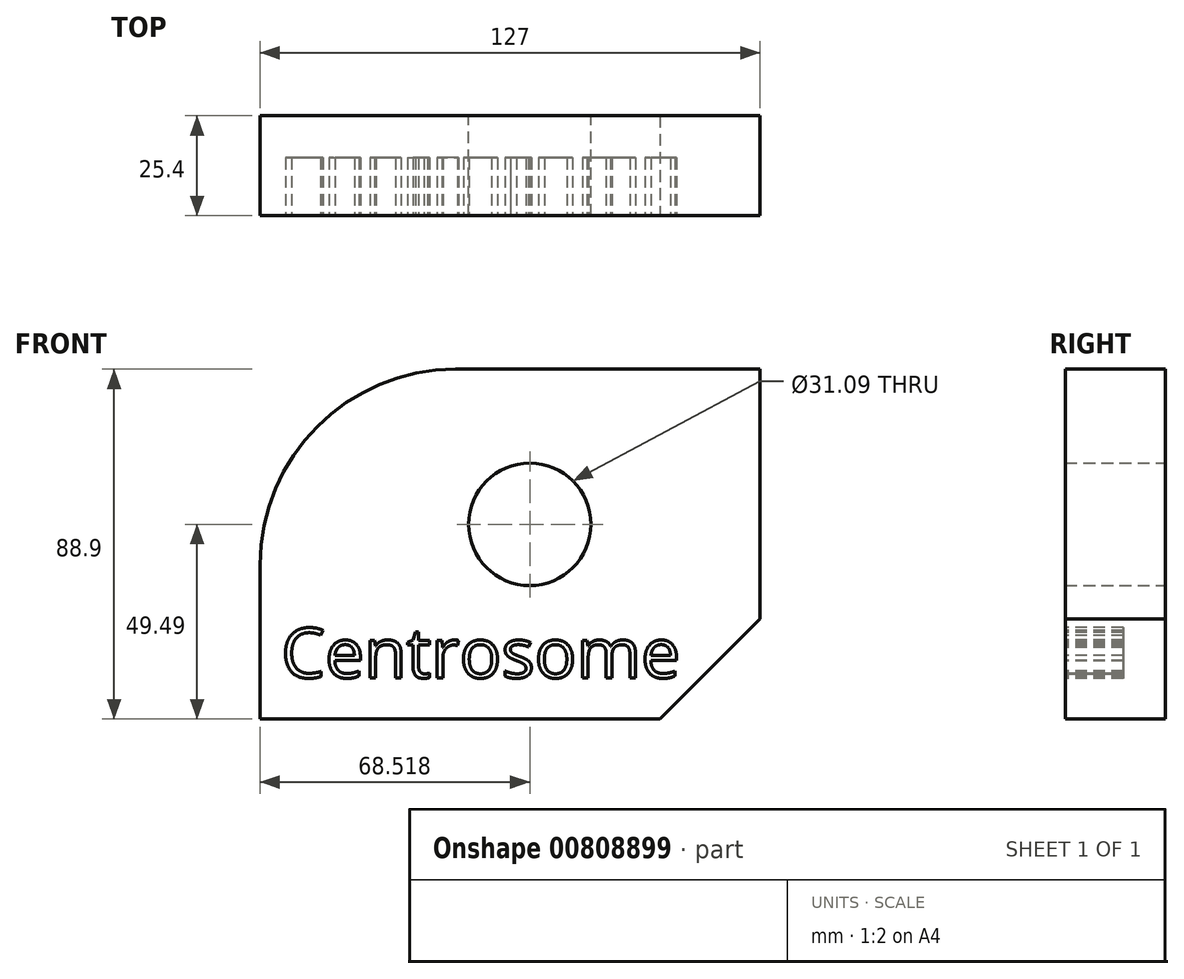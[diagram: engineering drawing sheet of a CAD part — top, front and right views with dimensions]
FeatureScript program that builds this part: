
annotation { "Feature Type Name" : "Feature", "Feature Type Description" : "" }
export const myFeature = defineFeature(function(context is Context, id is Id, definition is map)
    precondition{}
    {
        {
            var Q0;
            Q0=qCreatedBy(makeId("Front.planeOp"),FACE);
            var sketch = newSketch(context, id + "F0", { "sketchPlane" : qUnion([Q0])});
            skLineSegment(sketch, "E0.bottom", {"start": v(-62.51, 39.4) * mm, "end": v(64.49, 39.4) * mm});
            skLineSegment(sketch, "E0.top", {"start": v(-62.51, -49.5) * mm, "end": v(64.49, -49.5) * mm});
            skLineSegment(sketch, "E0.left", {"start": v(-62.51, 39.4) * mm, "end": v(-62.51, -49.5) * mm});
            skLineSegment(sketch, "E0.right", {"start": v(64.49, 39.4) * mm, "end": v(64.49, -49.5) * mm});
            skSolve(sketch);
        }
        {
            var Q0;
            Q0 = qSketchRegion(id + "F0", true);
            extrude(context, id + "F1", {"entities" : qUnion([Q0]), "depth" : 25.4 * mm, "offsetDistance" : 25.4 * mm});
        }
        {
            var Q0;
            Q0=makeQuery(id+"F1.opExtrude","SWEPT_EDGE",EDGE,{"disambiguationData":[OSD([sQuery(id+"F0.wireOp",EDGE,"E0.bottom"),sQuery(id+"F0.wireOp",EDGE,"E0.left")])]});
            fillet(context, id + "F2", {"entities" : qUnion([Q0]), "radius" : 49.67 * mm, "tangentPropagation" : true, "allowEdgeOverflow" : false});
        }
        {
            var Q0;
            Q0=makeQuery(id+"F1.opExtrude","SWEPT_EDGE",EDGE,{"disambiguationData":[OSD([sQuery(id+"F0.wireOp",EDGE,"E0.top"),sQuery(id+"F0.wireOp",EDGE,"E0.right")])]});
            chamfer(context, id + "F3", {"entities" : qUnion([Q0]), "width" : 25.4 * mm, "tangentPropagation" : true});
        }
        {
            var Q0;
            Q0=makeQuery(id+"F1.opExtrude","CAP_FACE",FACE,{"disambiguationData":[OSD([sQuery(id+"F0.wireOp",EDGE,"E0.bottom"),sQuery(id+"F0.wireOp",EDGE,"E0.top"),sQuery(id+"F0.wireOp",EDGE,"E0.left"),sQuery(id+"F0.wireOp",EDGE,"E0.right")])],"isStart":true});
            var sketch = newSketch(context, id + "F4", { "sketchPlane" : qUnion([Q0])});
            skCircle(sketch, "E1", {"center": v(-6, 0) * mm, "radius": 15.55 * mm});
            skSolve(sketch);
        }
        {
            var Q0;
            Q0 = qSketchRegion(id + "F4", true);
            extrude(context, id + "F5", {"entities" : qUnion([Q0]), "operationType" : NewBodyOperationType.REMOVE, "oppositeDirection" : true, "depth" : 38.1 * mm, "offsetDistance" : 25.4 * mm});
        }
        {
            var Q0;
            Q0=makeQuery(id+"F1.opExtrude","CAP_FACE",FACE,{"disambiguationData":[OSD([sQuery(id+"F0.wireOp",EDGE,"E0.bottom"),sQuery(id+"F0.wireOp",EDGE,"E0.top"),sQuery(id+"F0.wireOp",EDGE,"E0.left"),sQuery(id+"F0.wireOp",EDGE,"E0.right")])],"isStart":false});
            var sketch = newSketch(context, id + "F6", { "sketchPlane" : qUnion([Q0])});
            skText(sketch, "E2", { "text": "Centrosome", "fontName": "OpenSans-Regular.ttf"});
            const initialGuessF6  = {"E2": [-0.05712, -0.03898, 1, 0, 0.0127]};
            skSetInitialGuess(sketch, initialGuessF6);
            skSolve(sketch);
        }
        {
            var Q0;
            Q0 = qSketchRegion(id + "F6", true);
            extrude(context, id + "F7", {"entities" : qUnion([Q0]), "operationType" : NewBodyOperationType.REMOVE, "oppositeDirection" : true, "depth" : 14.73 * mm, "offsetDistance" : 25.4 * mm});
        }
    });
